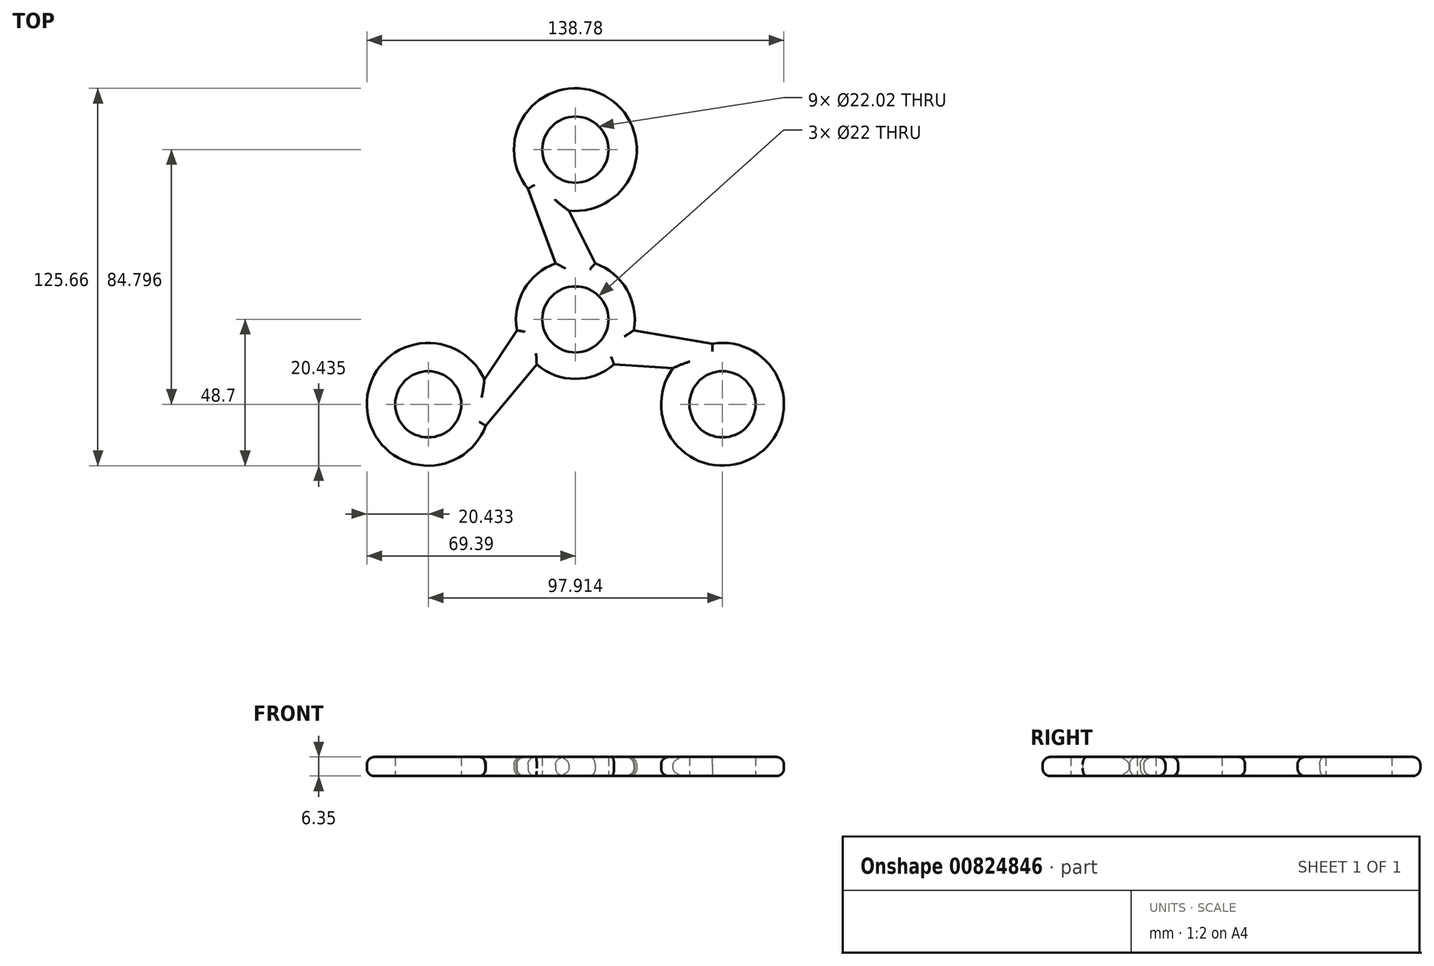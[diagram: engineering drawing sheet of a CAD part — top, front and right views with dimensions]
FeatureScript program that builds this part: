
annotation { "Feature Type Name" : "Feature", "Feature Type Description" : "" }
export const myFeature = defineFeature(function(context is Context, id is Id, definition is map)
    precondition{}
    {
        {
            var Q0;
            Q0=qCreatedBy(makeId("Top.planeOp"),FACE);
            var sketch = newSketch(context, id + "F0", { "sketchPlane" : qUnion([Q0])});
            skCircle(sketch, "E0", {"center": v(0, 0) * mm, "radius": 11 * mm});
            skCircle(sketch, "E1", {"center": v(0, 56.53) * mm, "radius": 11.01 * mm});
            skArc(sketch, "E2", {"start": v(-2.17, 36.21) * mm, "mid": v(9.68, 74.53) * mm, "end": v(-15.75, 43.51) * mm});
            skArc(sketch, "E3", {"start": v(-6.59, 18.65) * mm, "mid": v(-17.13, 9.9) * mm, "end": v(-19.45, -3.62) * mm});
            skLineSegment(sketch, "E4", {"start": v(-15.75, 43.51) * mm, "end": v(-6.59, 18.65) * mm});
            skLineSegment(sketch, "E5", {"start": v(6.59, 18.65) * mm, "end": v(-2.17, 36.21) * mm});
            skCircle(sketch, "E6.1.0", {"center": v(-48.96, -28.27) * mm, "radius": 11.01 * mm});
            skArc(sketch, "E6.1.1", {"start": v(-30.28, -19.99) * mm, "mid": v(-69.38, -28.89) * mm, "end": v(-29.8, -35.4) * mm});
            skLineSegment(sketch, "E6.1.2", {"start": v(-19.45, -3.62) * mm, "end": v(-30.28, -19.99) * mm});
            skLineSegment(sketch, "E6.1.3", {"start": v(-29.8, -35.4) * mm, "end": v(-12.86, -15.03) * mm});
            skCircle(sketch, "E6.2.0", {"center": v(48.96, -28.27) * mm, "radius": 11.01 * mm});
            skArc(sketch, "E6.2.1", {"start": v(32.45, -16.23) * mm, "mid": v(59.7, -45.64) * mm, "end": v(45.56, -8.12) * mm});
            skLineSegment(sketch, "E6.2.2", {"start": v(12.86, -15.03) * mm, "end": v(32.45, -16.23) * mm});
            skLineSegment(sketch, "E6.2.3", {"start": v(45.56, -8.12) * mm, "end": v(19.45, -3.62) * mm});
            skArc(sketch, "E7.trimOffspring", {"start": v(19.45, -3.62) * mm, "mid": v(17.13, 9.9) * mm, "end": v(6.59, 18.65) * mm});
            skArc(sketch, "E8.trimOffspring", {"start": v(-12.86, -15.03) * mm, "mid": v(0, -19.78) * mm, "end": v(12.86, -15.03) * mm});
            skSolve(sketch);
        }
        {
            var Q0;
            Q0 = qSketchRegion(id + "F0", true);
            extrude(context, id + "F1", {"entities" : qUnion([Q0]), "depth" : 6.35 * mm, "offsetDistance" : 25.4 * mm});
        }
        {
            var Q0;
            Q0=makeQuery(id+"F1.opExtrude","CAP_EDGE",EDGE,{"disambiguationData":[OSD([sQuery(id+"F0.wireOp",EDGE,"E8.trimOffspring")])],"isStart":false});
            var Q1;
            Q1=makeQuery(id+"F1.opExtrude","CAP_EDGE",EDGE,{"disambiguationData":[OSD([sQuery(id+"F0.wireOp",EDGE,"E6.1.3")])],"isStart":false});
            var Q2;
            Q2=makeQuery(id+"F1.opExtrude","CAP_EDGE",EDGE,{"disambiguationData":[OSD([sQuery(id+"F0.wireOp",EDGE,"E6.1.1")])],"isStart":false});
            var Q3;
            Q3=makeQuery(id+"F1.opExtrude","CAP_EDGE",EDGE,{"disambiguationData":[OSD([sQuery(id+"F0.wireOp",EDGE,"E3")])],"isStart":false});
            var Q4;
            Q4=makeQuery(id+"F1.opExtrude","CAP_EDGE",EDGE,{"disambiguationData":[OSD([sQuery(id+"F0.wireOp",EDGE,"E6.1.1")])],"isStart":true});
            var Q5;
            Q5=makeQuery(id+"F1.opExtrude","CAP_EDGE",EDGE,{"disambiguationData":[OSD([sQuery(id+"F0.wireOp",EDGE,"E6.1.2")])],"isStart":false});
            var Q6;
            Q6=makeQuery(id+"F1.opExtrude","CAP_EDGE",EDGE,{"disambiguationData":[OSD([sQuery(id+"F0.wireOp",EDGE,"E4")])],"isStart":false});
            var Q7;
            Q7=makeQuery(id+"F1.opExtrude","CAP_EDGE",EDGE,{"disambiguationData":[OSD([sQuery(id+"F0.wireOp",EDGE,"E5")])],"isStart":false});
            var Q8;
            Q8=makeQuery(id+"F1.opExtrude","CAP_EDGE",EDGE,{"disambiguationData":[OSD([sQuery(id+"F0.wireOp",EDGE,"E2")])],"isStart":false});
            var Q9;
            Q9=makeQuery(id+"F1.opExtrude","CAP_EDGE",EDGE,{"disambiguationData":[OSD([sQuery(id+"F0.wireOp",EDGE,"E6.2.3")])],"isStart":false});
            var Q10;
            Q10=makeQuery(id+"F1.opExtrude","CAP_EDGE",EDGE,{"disambiguationData":[OSD([sQuery(id+"F0.wireOp",EDGE,"E6.2.2")])],"isStart":false});
            var Q11;
            Q11=makeQuery(id+"F1.opExtrude","CAP_EDGE",EDGE,{"disambiguationData":[OSD([sQuery(id+"F0.wireOp",EDGE,"E6.2.1")])],"isStart":false});
            var Q12;
            Q12=makeQuery(id+"F1.opExtrude","CAP_EDGE",EDGE,{"disambiguationData":[OSD([sQuery(id+"F0.wireOp",EDGE,"E7.trimOffspring")])],"isStart":false});
            var Q13;
            Q13=makeQuery(id+"F1.opExtrude","CAP_EDGE",EDGE,{"disambiguationData":[OSD([sQuery(id+"F0.wireOp",EDGE,"E2")])],"isStart":true});
            var Q14;
            Q14=makeQuery(id+"F1.opExtrude","CAP_EDGE",EDGE,{"disambiguationData":[OSD([sQuery(id+"F0.wireOp",EDGE,"E4")])],"isStart":true});
            var Q15;
            Q15=makeQuery(id+"F1.opExtrude","CAP_EDGE",EDGE,{"disambiguationData":[OSD([sQuery(id+"F0.wireOp",EDGE,"E5")])],"isStart":true});
            var Q16;
            Q16=makeQuery(id+"F1.opExtrude","CAP_EDGE",EDGE,{"disambiguationData":[OSD([sQuery(id+"F0.wireOp",EDGE,"E7.trimOffspring")])],"isStart":true});
            var Q17;
            Q17=makeQuery(id+"F1.opExtrude","CAP_EDGE",EDGE,{"disambiguationData":[OSD([sQuery(id+"F0.wireOp",EDGE,"E3")])],"isStart":true});
            var Q18;
            Q18=makeQuery(id+"F1.opExtrude","CAP_EDGE",EDGE,{"disambiguationData":[OSD([sQuery(id+"F0.wireOp",EDGE,"E6.1.2")])],"isStart":true});
            var Q19;
            Q19=makeQuery(id+"F1.opExtrude","CAP_EDGE",EDGE,{"disambiguationData":[OSD([sQuery(id+"F0.wireOp",EDGE,"E6.2.3")])],"isStart":true});
            var Q20;
            Q20=makeQuery(id+"F1.opExtrude","CAP_EDGE",EDGE,{"disambiguationData":[OSD([sQuery(id+"F0.wireOp",EDGE,"E6.2.1")])],"isStart":true});
            var Q21;
            Q21=makeQuery(id+"F1.opExtrude","CAP_EDGE",EDGE,{"disambiguationData":[OSD([sQuery(id+"F0.wireOp",EDGE,"E8.trimOffspring")])],"isStart":true});
            var Q22;
            Q22=makeQuery(id+"F1.opExtrude","CAP_EDGE",EDGE,{"disambiguationData":[OSD([sQuery(id+"F0.wireOp",EDGE,"E6.2.2")])],"isStart":true});
            var Q23;
            Q23=makeQuery(id+"F1.opExtrude","CAP_EDGE",EDGE,{"disambiguationData":[OSD([sQuery(id+"F0.wireOp",EDGE,"E6.1.3")])],"isStart":true});
            fillet(context, id + "F2", {"entities" : qUnion([Q0, Q1, Q2, Q3, Q4, Q5, Q6, Q7, Q8, Q9, Q10, Q11, Q12, Q13, Q14, Q15, Q16, Q17, Q18, Q19, Q20, Q21, Q22, Q23]), "radius" : 2.54 * mm, "tangentPropagation" : true, "allowEdgeOverflow" : false});
        }
    });
